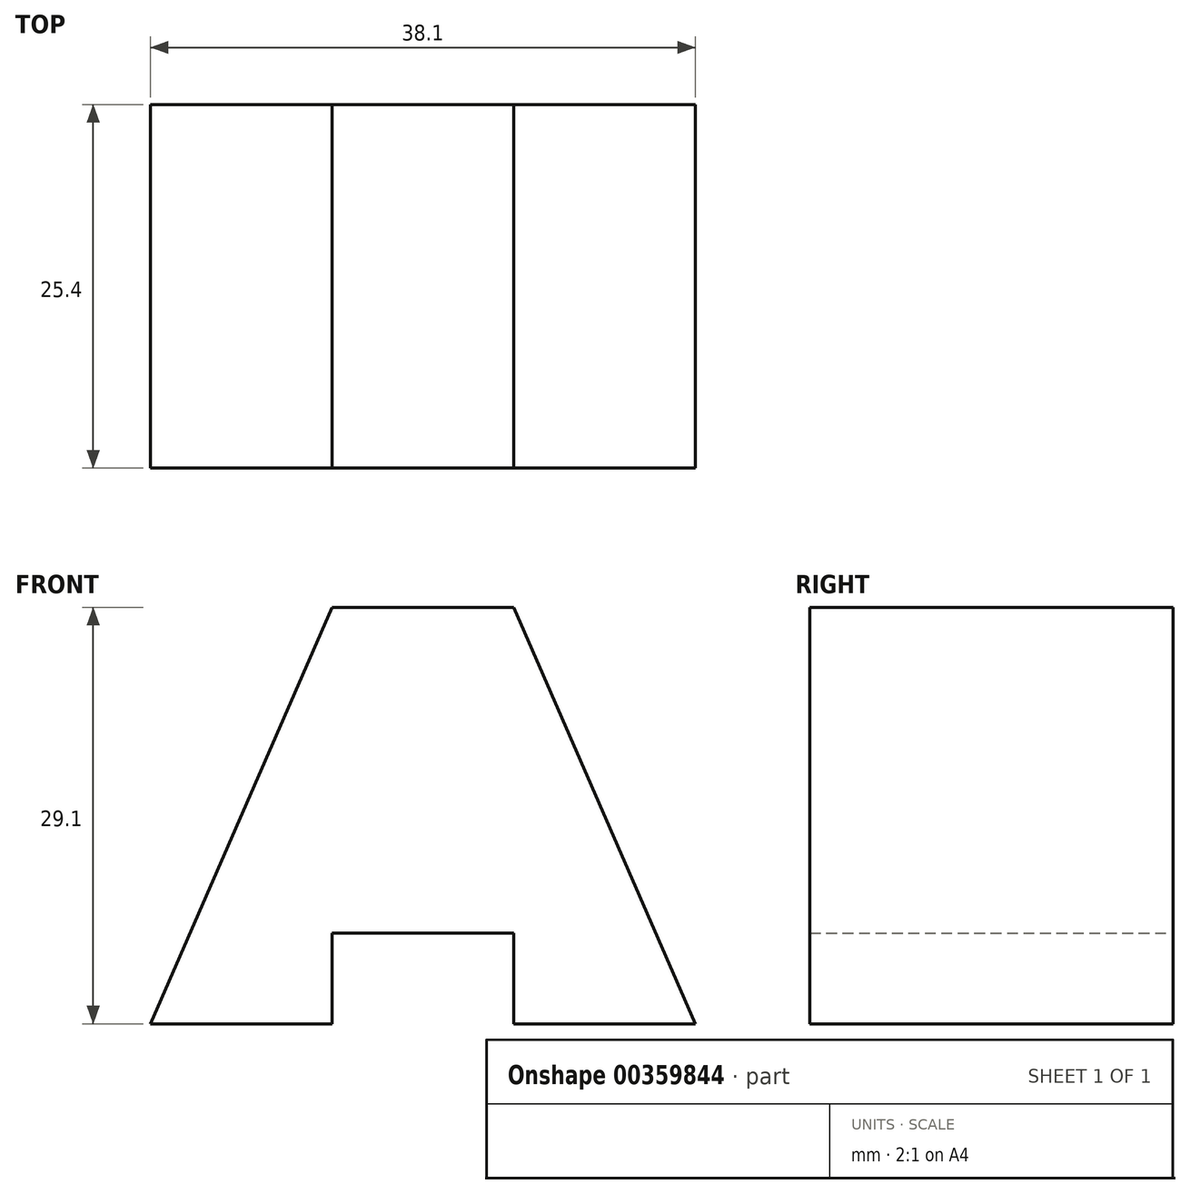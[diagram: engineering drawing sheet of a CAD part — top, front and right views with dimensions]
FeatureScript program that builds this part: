
annotation { "Feature Type Name" : "Feature", "Feature Type Description" : "" }
export const myFeature = defineFeature(function(context is Context, id is Id, definition is map)
    precondition{}
    {
        {
            var Q0;
            Q0=qCreatedBy(makeId("Front.planeOp"),FACE);
            var sketch = newSketch(context, id + "F0", { "sketchPlane" : qUnion([Q0])});
            skLineSegment(sketch, "E0", {"start": v(0, 0) * mm, "end": v(-12.7, 29.1) * mm});
            skLineSegment(sketch, "E1", {"start": v(-12.7, 29.1) * mm, "end": v(-25.4, 29.1) * mm});
            skLineSegment(sketch, "E2", {"start": v(-25.4, 29.1) * mm, "end": v(-38.1, 0) * mm});
            skLineSegment(sketch, "E3", {"start": v(-38.1, 0) * mm, "end": v(-25.4, 0) * mm});
            skLineSegment(sketch, "E4", {"start": v(-25.4, 0) * mm, "end": v(-25.4, 6.35) * mm});
            skLineSegment(sketch, "E5", {"start": v(-25.4, 6.35) * mm, "end": v(-12.7, 6.35) * mm});
            skLineSegment(sketch, "E6", {"start": v(-12.7, 6.35) * mm, "end": v(-12.7, 0) * mm});
            skLineSegment(sketch, "E7", {"start": v(-12.7, 0) * mm, "end": v(0, 0) * mm});
            skSolve(sketch);
        }
        {
            var Q0;
            Q0 = qSketchRegion(id + "F0", true);
            extrude(context, id + "F1", {"entities" : qUnion([Q0]), "depth" : 25.4 * mm});
        }
    });
